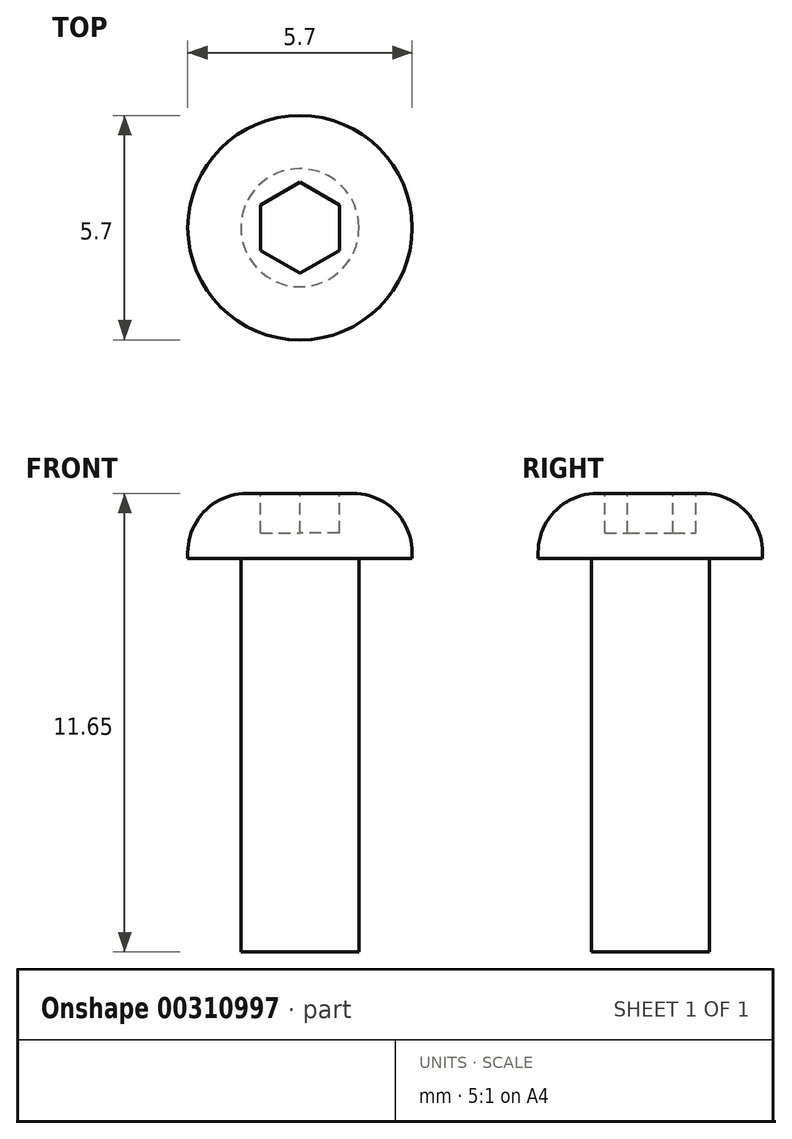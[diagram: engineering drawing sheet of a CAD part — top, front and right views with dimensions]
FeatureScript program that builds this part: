
annotation { "Feature Type Name" : "Feature", "Feature Type Description" : "" }
export const myFeature = defineFeature(function(context is Context, id is Id, definition is map)
    precondition{}
    {
        {
            var Q0;
            Q0=qCreatedBy(makeId("Top.planeOp"),FACE);
            var sketch = newSketch(context, id + "F0", { "sketchPlane" : qUnion([Q0])});
            skCircle(sketch, "E0", {"center": v(0, 0) * mm, "radius": 2.85 * mm});
            skCircle(sketch, "E1", {"center": v(0, 0) * mm, "radius": 1.5 * mm});
            skSolve(sketch);
        }
        {
            var Q0;
            Q0=makeQuery(id+"F0.imprint","IMPRINT",FACE,{"disambiguationData":[TD([[makeQuery(id+"F0.imprint","IMPRINT",EDGE,{"derivedFrom":sQuery(id+"F0.wireOp",EDGE,"E1")}),1.0]])]});
            extrude(context, id + "F1", {"entities" : qUnion([Q0]), "oppositeDirection" : true, "depth" : 10 * mm});
        }
        {
            var Q0;
            Q0=qSketchRegion(id+"F0",true);
            var Q1;
            Q1=makeQuery(id+"F1.opExtrude","CAP_FACE",FACE,{"disambiguationData":[OSD([sQuery(id+"F0.wireOp",EDGE,"E1")])],"isStart":true});
            extrude(context, id + "F2", {"entities" : qUnion([Q0, Q1]), "operationType" : NewBodyOperationType.ADD, "depth" : 1.65 * mm});
        }
        {
            var Q0;
            {var subQ0=sQuery(id+"F0.wireOp",EDGE,"E1");Q0=makeQuery(id+"F2.boolean.opBoolean","MERGE",FACE,{"derivedFrom":[makeQuery(id+"F2.opExtrude","CAP_FACE",FACE,{"disambiguationData":[OSD([sQuery(id+"F0.wireOp",EDGE,"E0"),subQ0])],"isStart":false}),makeQuery(id+"F2.opExtrude","CAP_FACE",FACE,{"disambiguationData":[OSD([subQ0])],"isStart":false})]});}
            var sketch = newSketch(context, id + "F3", { "sketchPlane" : qUnion([Q0])});
            skCircle(sketch, "E2.cCircle", {"center": v(0, 0) * mm, "radius": 1 * mm, "construction": true});
            skLineSegment(sketch, "E2.0", {"start": v(-1, 0.58) * mm, "end": v(0, 1.15) * mm});
            skLineSegment(sketch, "E2.1", {"start": v(0, 1.15) * mm, "end": v(1, 0.58) * mm});
            skLineSegment(sketch, "E2.2", {"start": v(1, 0.58) * mm, "end": v(1, -0.58) * mm});
            skLineSegment(sketch, "E2.3", {"start": v(1, -0.58) * mm, "end": v(0, -1.15) * mm});
            skLineSegment(sketch, "E2.4", {"start": v(0, -1.15) * mm, "end": v(-1, -0.58) * mm});
            skLineSegment(sketch, "E2.5", {"start": v(-1, -0.58) * mm, "end": v(-1, 0.58) * mm});
            skPoint(sketch, "E2.0.midPoint", {"position": v(-0.5, 0.87) * mm});
            skSolve(sketch);
        }
        {
            var Q0;
            Q0=qSketchRegion(id+"F3",true);
            extrude(context, id + "F4", {"entities" : qUnion([Q0]), "operationType" : NewBodyOperationType.REMOVE, "oppositeDirection" : true, "depth" : 1 * mm});
        }
        {
            var Q0;
            Q0=makeQuery(id+"F2.opExtrude","CAP_EDGE",EDGE,{"disambiguationData":[OSD([sQuery(id+"F0.wireOp",EDGE,"E0")])],"isStart":false});
            fillet(context, id + "F5", {"entities" : qUnion([Q0]), "radius" : 1.5 * mm, "tangentPropagation" : true, "allowEdgeOverflow" : false});
        }
    });
